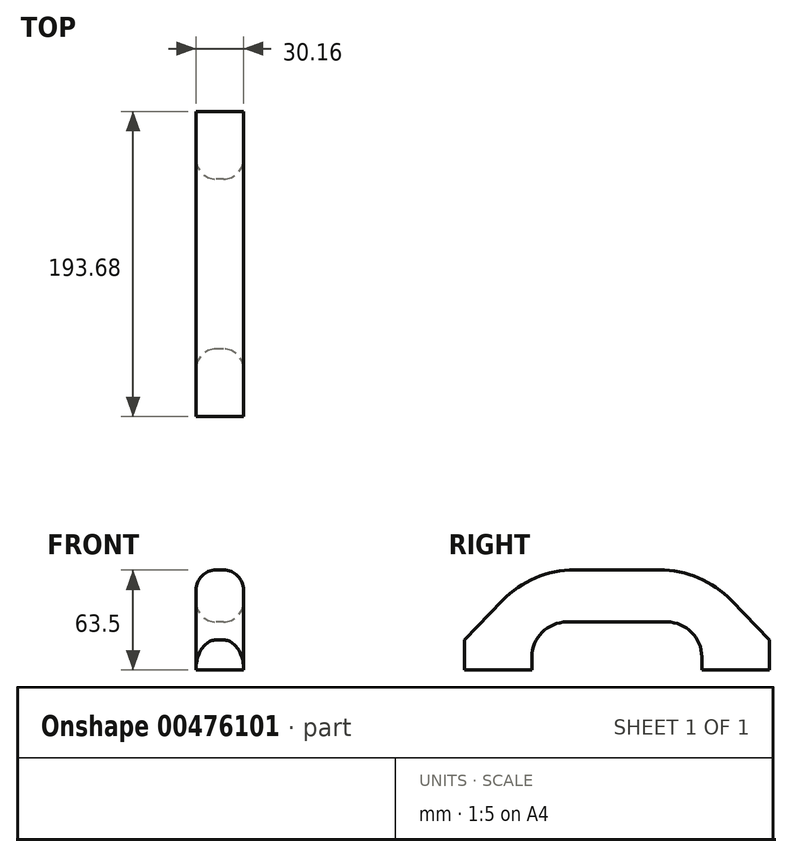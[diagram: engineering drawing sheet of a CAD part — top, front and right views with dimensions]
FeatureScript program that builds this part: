
annotation { "Feature Type Name" : "Feature", "Feature Type Description" : "" }
export const myFeature = defineFeature(function(context is Context, id is Id, definition is map)
    precondition{}
    {
        {
            var Q0;
            Q0=qCreatedBy(makeId("Right.planeOp"),FACE);
            var sketch = newSketch(context, id + "F0", { "sketchPlane" : qUnion([Q0])});
            skLineSegment(sketch, "E0", {"start": v(0, 0) * mm, "end": v(42.86, 0) * mm});
            skLineSegment(sketch, "E1", {"start": v(0, 0) * mm, "end": v(0, 19.05) * mm});
            skLineSegment(sketch, "E2", {"start": v(193.68, 0) * mm, "end": v(193.68, 19.05) * mm});
            skLineSegment(sketch, "E3", {"start": v(42.86, 63.5) * mm, "end": v(150.8, 63.5) * mm});
            skPoint(sketch, "E4", {"position": v(0, 19.05) * mm});
            skPoint(sketch, "E5", {"position": v(193.68, 19.05) * mm});
            skPoint(sketch, "E6", {"position": v(42.86, 0) * mm});
            skPoint(sketch, "E7", {"position": v(150.8, 0) * mm});
            skPoint(sketch, "E8", {"position": v(96.84, 63.5) * mm});
            skLineSegment(sketch, "E9", {"start": v(96.84, 107.02) * mm, "end": v(96.84, -32.56) * mm, "construction": true});
            skPoint(sketch, "E10", {"position": v(96.84, 30.48) * mm});
            skLineSegment(sketch, "E11", {"start": v(96.84, 30.48) * mm, "end": v(42.86, 30.48) * mm});
            skLineSegment(sketch, "E12", {"start": v(42.86, 0) * mm, "end": v(42.86, 30.48) * mm});
            skLineSegment(sketch, "E13", {"start": v(96.84, 30.48) * mm, "end": v(150.8, 30.48) * mm});
            skLineSegment(sketch, "E14", {"start": v(150.8, 0) * mm, "end": v(150.8, 30.48) * mm});
            skLineSegment(sketch, "E15", {"start": v(0, 19.05) * mm, "end": v(42.86, 63.5) * mm});
            skLineSegment(sketch, "E16", {"start": v(193.68, 19.05) * mm, "end": v(150.8, 63.5) * mm});
            skLineSegment(sketch, "E17.trimOffspring", {"start": v(150.8, 0) * mm, "end": v(193.68, 0) * mm});
            skSolve(sketch);
        }
        {
            var Q0;
            Q0=makeQuery(id+"F0.imprint","IMPRINT",FACE,{"disambiguationData":[TD([[makeQuery(id+"F0.imprint","IMPRINT",EDGE,{"derivedFrom":sQuery(id+"F0.wireOp",EDGE,"E0")}),1.0]])]});
            extrude(context, id + "F1", {"entities" : qUnion([Q0]), "depth" : 15.08 * mm, "hasSecondDirection" : true, "secondDirectionOppositeDirection" : true, "secondDirectionDepth" : 15.08 * mm});
        }
        {
            var Q0;
            Q0=makeQuery(id+"F1.opExtrude","SWEPT_EDGE",EDGE,{"disambiguationData":[OSD([sQuery(id+"F0.wireOp",EDGE,"E3"),sQuery(id+"F0.wireOp",EDGE,"E15")])]});
            var Q1;
            Q1=makeQuery(id+"F1.opExtrude","SWEPT_EDGE",EDGE,{"disambiguationData":[OSD([sQuery(id+"F0.wireOp",EDGE,"E3"),sQuery(id+"F0.wireOp",EDGE,"E16")])]});
            fillet(context, id + "F2", {"entities" : qUnion([Q0, Q1]), "radius" : 63.5 * mm, "tangentPropagation" : true, "allowEdgeOverflow" : false});
        }
        {
            var Q0;
            Q0=makeQuery(id+"F1.opExtrude","SWEPT_EDGE",EDGE,{"disambiguationData":[OSD([sQuery(id+"F0.wireOp",EDGE,"E11"),sQuery(id+"F0.wireOp",EDGE,"E12")])]});
            var Q1;
            Q1=makeQuery(id+"F1.opExtrude","SWEPT_EDGE",EDGE,{"disambiguationData":[OSD([sQuery(id+"F0.wireOp",EDGE,"E13"),sQuery(id+"F0.wireOp",EDGE,"E14")])]});
            fillet(context, id + "F3", {"entities" : qUnion([Q0, Q1]), "radius" : 22.22 * mm, "tangentPropagation" : true, "allowEdgeOverflow" : false});
        }
        {
            var Q0;
            Q0=makeQuery(id+"F1.opExtrude","CAP_EDGE",EDGE,{"disambiguationData":[OSD([sQuery(id+"F0.wireOp",EDGE,"E11"),sQuery(id+"F0.wireOp",EDGE,"E13")])],"isStart":false});
            var Q1;
            Q1=makeQuery(id+"F1.opExtrude","CAP_EDGE",EDGE,{"disambiguationData":[OSD([sQuery(id+"F0.wireOp",EDGE,"E11"),sQuery(id+"F0.wireOp",EDGE,"E13")])],"isStart":true});
            var Q2;
            Q2=makeQuery(id+"F1.opExtrude","CAP_EDGE",EDGE,{"disambiguationData":[OSD([sQuery(id+"F0.wireOp",EDGE,"E3")])],"isStart":true});
            var Q3;
            Q3=makeQuery(id+"F1.opExtrude","CAP_EDGE",EDGE,{"disambiguationData":[OSD([sQuery(id+"F0.wireOp",EDGE,"E3")])],"isStart":false});
            fillet(context, id + "F4", {"entities" : qUnion([Q0, Q1, Q2, Q3]), "radius" : 12.7 * mm, "tangentPropagation" : true, "allowEdgeOverflow" : false});
        }
    });
